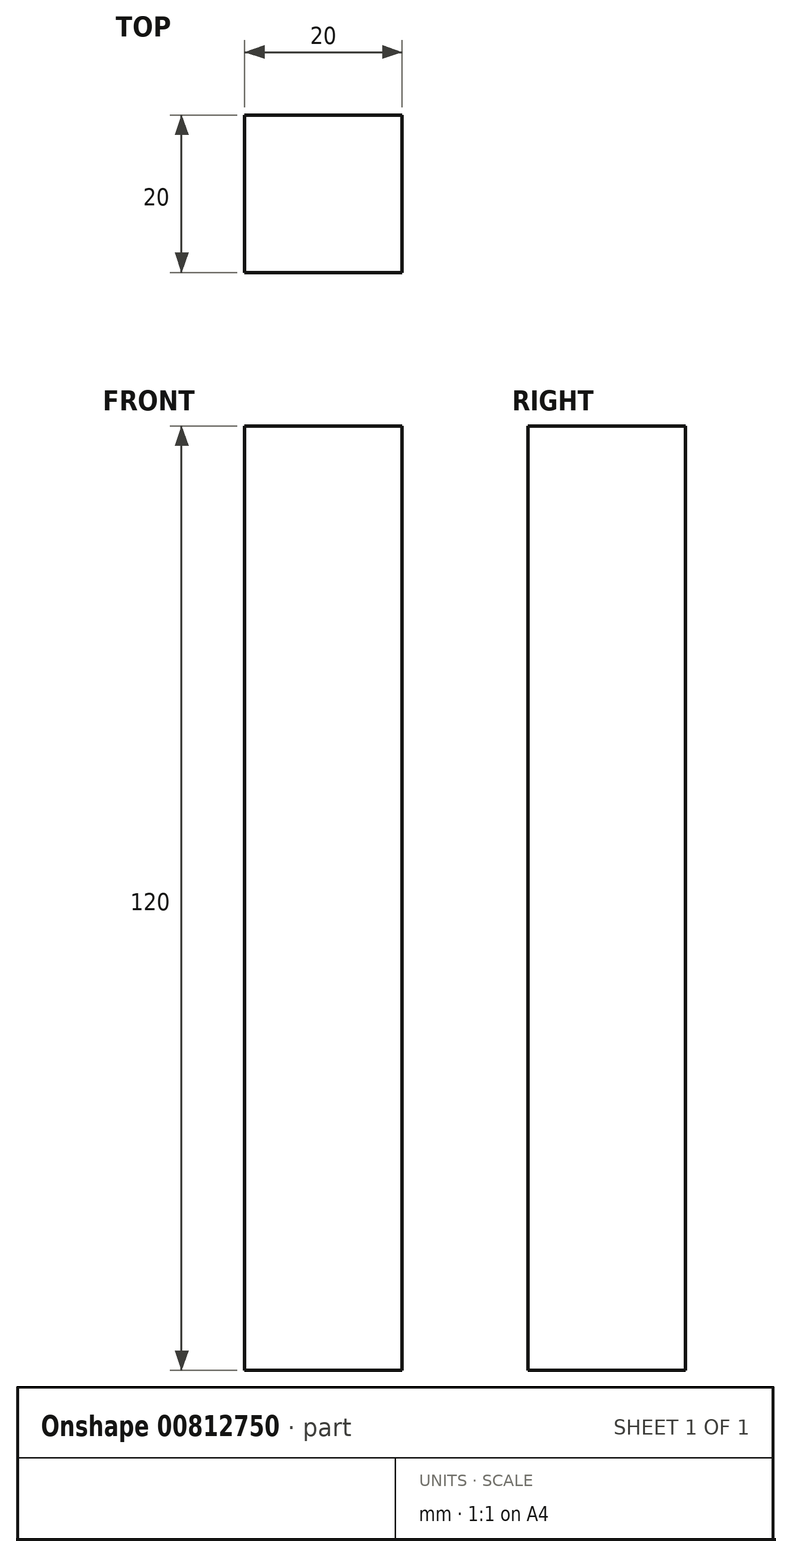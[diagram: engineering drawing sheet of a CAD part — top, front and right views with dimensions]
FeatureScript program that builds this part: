
annotation { "Feature Type Name" : "Feature", "Feature Type Description" : "" }
export const myFeature = defineFeature(function(context is Context, id is Id, definition is map)
    precondition{}
    {
        {
            var Q0;
            Q0=qCreatedBy(makeId("Top.planeOp"),FACE);
            var sketch = newSketch(context, id + "F0", { "sketchPlane" : qUnion([Q0])});
            skLineSegment(sketch, "E0.bottom", {"start": v(-10, 10) * mm, "end": v(10, 10) * mm});
            skLineSegment(sketch, "E0.top", {"start": v(-10, -10) * mm, "end": v(10, -10) * mm});
            skLineSegment(sketch, "E0.left", {"start": v(-10, 10) * mm, "end": v(-10, -10) * mm});
            skLineSegment(sketch, "E0.right", {"start": v(10, 10) * mm, "end": v(10, -10) * mm});
            skSolve(sketch);
        }
        {
            var Q0;
            Q0 = qSketchRegion(id + "F0", true);
            extrude(context, id + "F1", {"entities" : qUnion([Q0]), "depth" : 120 * mm, "offsetDistance" : 25 * mm});
        }
    });
